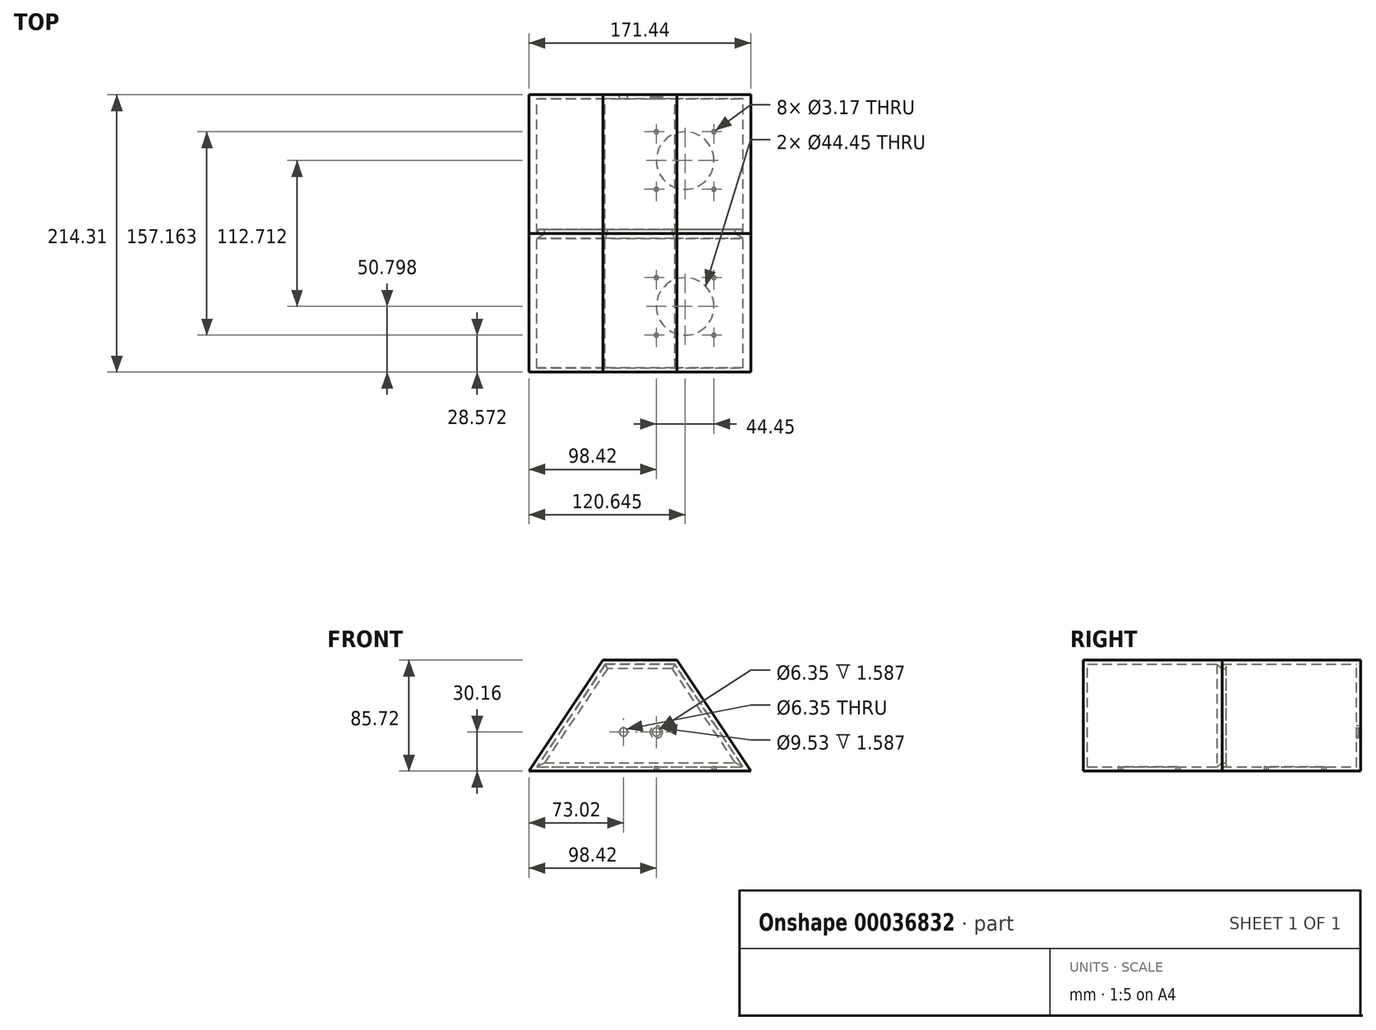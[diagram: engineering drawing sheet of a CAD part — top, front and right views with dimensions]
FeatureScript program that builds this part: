
annotation { "Feature Type Name" : "Feature", "Feature Type Description" : "" }
export const myFeature = defineFeature(function(context is Context, id is Id, definition is map)
    precondition{}
    {
        {
            var Q0;
            Q0=qCreatedBy(makeId("Front.planeOp"),FACE);
            var sketch = newSketch(context, id + "F0", { "sketchPlane" : qUnion([Q0])});
            skLineSegment(sketch, "E0", {"start": v(-85.73, -42.86) * mm, "end": v(85.73, -42.86) * mm});
            skLineSegment(sketch, "E1", {"start": v(85.73, -42.86) * mm, "end": v(28.57, 42.86) * mm});
            skLineSegment(sketch, "E2", {"start": v(28.58, 42.86) * mm, "end": v(-28.58, 42.86) * mm});
            skLineSegment(sketch, "E3", {"start": v(-28.57, 42.86) * mm, "end": v(-85.73, -42.86) * mm});
            skLineSegment(sketch, "E4", {"start": v(0, 42.86) * mm, "end": v(0, -42.86) * mm});
            skPoint(sketch, "E4.endSnap0", {"position": v(0, -42.86) * mm});
            skPoint(sketch, "E5", {"position": v(0, 0) * mm});
            skSolve(sketch);
        }
        {
            var Q0;
            {var subQ2=sQuery(id+"F0.wireOp",EDGE,"E1");Q0=makeQuery(id+"F0.imprint","IMPRINT",FACE,{"disambiguationData":[TD([[makeQuery(id+"F0.imprint","IMPRINT",EDGE,{"derivedFrom":subQ2}),1.0]])]});}
            var Q1;
            {var subQ1=sQuery(id+"F0.wireOp",EDGE,"E3");Q1=makeQuery(id+"F0.imprint","IMPRINT",FACE,{"disambiguationData":[TD([[makeQuery(id+"F0.imprint","IMPRINT",EDGE,{"derivedFrom":subQ1}),1.0]])]});}
            extrude(context, id + "F1", {"entities" : qUnion([Q0, Q1]), "depth" : 214.3 * mm});
        }
        {
            var Q0;
            Q0=makeQuery(id+"F1.opExtrude","CAP_FACE",FACE,{"disambiguationData":[OSD([sQuery(id+"F0.wireOp",EDGE,"E0"),sQuery(id+"F0.wireOp",EDGE,"E1"),sQuery(id+"F0.wireOp",EDGE,"E2"),sQuery(id+"F0.wireOp",EDGE,"E3")])],"isStart":true});
            shell(context, id + "F2", {"entities" : qUnion([Q0]), "thickness" : 3.17 * mm});
        }
        {
            var Q0;
            Q0=qCreatedBy(makeId("Front.planeOp"),FACE);
            var sketch = newSketch(context, id + "F3", { "sketchPlane" : qUnion([Q0])});
            skLineSegment(sketch, "E6.0.0", {"start": v(-28.57, 42.86) * mm, "end": v(28.57, 42.86) * mm});
            skLineSegment(sketch, "E6.0.1", {"start": v(28.57, 42.86) * mm, "end": v(85.72, -42.86) * mm});
            skLineSegment(sketch, "E6.0.2", {"start": v(85.72, -42.86) * mm, "end": v(-85.73, -42.86) * mm});
            skLineSegment(sketch, "E6.0.3", {"start": v(-85.73, -42.86) * mm, "end": v(-28.57, 42.86) * mm});
            skSolve(sketch);
        }
        {
            var Q0;
            Q0 = qSketchRegion(id + "F3", true);
            extrude(context, id + "F4", {"entities" : qUnion([Q0]), "operationType" : NewBodyOperationType.ADD, "depth" : 3.17 * mm});
        }
        {
            var Q0;
            Q0=makeQuery(id+"F1.opExtrude","SWEPT_FACE",FACE,{"disambiguationData":[OSD([sQuery(id+"F0.wireOp",EDGE,"E0")])]});
            var sketch = newSketch(context, id + "F5", { "sketchPlane" : qUnion([Q0])});
            skLineSegment(sketch, "E7", {"start": v(85.72, 214.31) * mm, "end": v(34.92, 214.31) * mm, "construction": true});
            skLineSegment(sketch, "E8", {"start": v(34.92, 214.31) * mm, "end": v(34.92, 163.51) * mm, "construction": true});
            skLineSegment(sketch, "E9", {"start": v(85.72, 0) * mm, "end": v(34.92, 0) * mm, "construction": true});
            skLineSegment(sketch, "E10", {"start": v(34.92, 0) * mm, "end": v(34.92, 50.8) * mm, "construction": true});
            skPoint(sketch, "E11", {"position": v(34.92, 50.8) * mm});
            skPoint(sketch, "E12", {"position": v(34.92, 163.51) * mm});
            skLineSegment(sketch, "E13", {"start": v(34.92, 163.51) * mm, "end": v(57.15, 163.51) * mm, "construction": true});
            skLineSegment(sketch, "E14", {"start": v(57.15, 163.51) * mm, "end": v(57.15, 185.74) * mm, "construction": true});
            skLineSegment(sketch, "E15", {"start": v(57.15, 185.74) * mm, "end": v(12.7, 185.74) * mm, "construction": true});
            skLineSegment(sketch, "E16", {"start": v(12.7, 185.74) * mm, "end": v(12.7, 141.29) * mm, "construction": true});
            skLineSegment(sketch, "E17", {"start": v(12.7, 141.29) * mm, "end": v(57.15, 141.29) * mm, "construction": true});
            skLineSegment(sketch, "E18.rect.bottom", {"start": v(57.15, 28.58) * mm, "end": v(12.7, 28.57) * mm, "construction": true});
            skLineSegment(sketch, "E18.rect.top", {"start": v(57.15, 73.03) * mm, "end": v(12.7, 73.03) * mm, "construction": true});
            skLineSegment(sketch, "E18.rect.left", {"start": v(57.15, 28.58) * mm, "end": v(57.15, 73.03) * mm, "construction": true});
            skLineSegment(sketch, "E18.rect.right", {"start": v(12.7, 28.57) * mm, "end": v(12.7, 73.03) * mm, "construction": true});
            skCircle(sketch, "E19", {"center": v(57.15, 73.03) * mm, "radius": 1.59 * mm});
            skCircle(sketch, "E20", {"center": v(57.15, 28.58) * mm, "radius": 1.59 * mm});
            skCircle(sketch, "E21", {"center": v(12.7, 28.57) * mm, "radius": 1.59 * mm});
            skCircle(sketch, "E22", {"center": v(12.7, 73.03) * mm, "radius": 1.59 * mm});
            skCircle(sketch, "E23", {"center": v(12.7, 185.74) * mm, "radius": 1.59 * mm});
            skCircle(sketch, "E24", {"center": v(57.15, 185.74) * mm, "radius": 1.59 * mm});
            skCircle(sketch, "E25", {"center": v(57.15, 141.29) * mm, "radius": 1.59 * mm});
            skCircle(sketch, "E26", {"center": v(12.7, 141.29) * mm, "radius": 1.59 * mm});
            skSolve(sketch);
        }
        {
            var Q0;
            Q0=sQuery(id+"F5.wireOp",VERTEX,"E11");
            var Q1;
            Q1=sQuery(id+"F5.wireOp",VERTEX,"E12");
            var Q2;
            Q2=makeQuery(id+"F1.opExtrude","SWEPT_BODY",BODY,{"disambiguationData":[OSD([sQuery(id+"F0.wireOp",EDGE,"E0"),sQuery(id+"F0.wireOp",EDGE,"E1"),sQuery(id+"F0.wireOp",EDGE,"E2"),sQuery(id+"F0.wireOp",EDGE,"E3")])]});
            hole(context, id + "F6", {"style" : HoleStyle.SIMPLE, "holeDiameter" : 44.45 * mm, "endStyle" : HoleEndStyle.BLIND, "holeDepth" : 3.17 * mm, "locations" : qUnion([Q0, Q1]), "scope" : qUnion([Q2])});
        }
        {
            var Q0;
            Q0=makeQuery(id+"F4.boolean.opBoolean","MERGE",FACE,{"derivedFrom":[makeQuery(id+"F1.opExtrude","CAP_FACE",FACE,{"disambiguationData":[OSD([sQuery(id+"F0.wireOp",EDGE,"E0"),sQuery(id+"F0.wireOp",EDGE,"E1"),sQuery(id+"F0.wireOp",EDGE,"E2"),sQuery(id+"F0.wireOp",EDGE,"E3")])],"isStart":true}),makeQuery(id+"F4.opExtrude","CAP_FACE",FACE,{"disambiguationData":[OSD([sQuery(id+"F3.wireOp",EDGE,"E6.0.0"),sQuery(id+"F3.wireOp",EDGE,"E6.0.1"),sQuery(id+"F3.wireOp",EDGE,"E6.0.2"),sQuery(id+"F3.wireOp",EDGE,"E6.0.3")])],"isStart":true})]});
            var sketch = newSketch(context, id + "F7", { "sketchPlane" : qUnion([Q0])});
            skCircle(sketch, "E27", {"center": v(12.7, -12.7) * mm, "radius": 3.18 * mm});
            skSolve(sketch);
        }
        {
            var Q0;
            Q0 = qSketchRegion(id + "F7", true);
            extrude(context, id + "F8", {"entities" : qUnion([Q0]), "operationType" : NewBodyOperationType.REMOVE, "oppositeDirection" : true, "depth" : 25.4 * mm});
        }
        {
            var Q0;
            Q0=makeQuery(id+"F4.boolean.opBoolean","MERGE",FACE,{"derivedFrom":[makeQuery(id+"F1.opExtrude","CAP_FACE",FACE,{"disambiguationData":[OSD([sQuery(id+"F0.wireOp",EDGE,"E0"),sQuery(id+"F0.wireOp",EDGE,"E1"),sQuery(id+"F0.wireOp",EDGE,"E2"),sQuery(id+"F0.wireOp",EDGE,"E3")])],"isStart":true}),makeQuery(id+"F4.opExtrude","CAP_FACE",FACE,{"disambiguationData":[OSD([sQuery(id+"F3.wireOp",EDGE,"E6.0.0"),sQuery(id+"F3.wireOp",EDGE,"E6.0.1"),sQuery(id+"F3.wireOp",EDGE,"E6.0.2"),sQuery(id+"F3.wireOp",EDGE,"E6.0.3")])],"isStart":true})]});
            var sketch = newSketch(context, id + "F9", { "sketchPlane" : qUnion([Q0])});
            skCircle(sketch, "E28", {"center": v(-12.7, -12.7) * mm, "radius": 3.18 * mm});
            skSolve(sketch);
        }
        {
            var Q0;
            Q0 = qSketchRegion(id + "F9", true);
            extrude(context, id + "F10", {"entities" : qUnion([Q0]), "operationType" : NewBodyOperationType.REMOVE, "oppositeDirection" : true, "depth" : 25.4 * mm});
        }
        {
            var Q0;
            Q0 = qSketchRegion(id + "F5", true);
            extrude(context, id + "F11", {"entities" : qUnion([Q0]), "operationType" : NewBodyOperationType.REMOVE, "oppositeDirection" : true, "depth" : 12.7 * mm});
        }
        {
            var Q0;
            Q0=makeQuery(id+"F4.opExtrude","CAP_FACE",FACE,{"disambiguationData":[OSD([sQuery(id+"F3.wireOp",EDGE,"E6.0.0"),sQuery(id+"F3.wireOp",EDGE,"E6.0.1"),sQuery(id+"F3.wireOp",EDGE,"E6.0.2"),sQuery(id+"F3.wireOp",EDGE,"E6.0.3")])],"isStart":false});
            var sketch = newSketch(context, id + "F12", { "sketchPlane" : qUnion([Q0])});
            skCircle(sketch, "E29", {"center": v(12.7, -12.7) * mm, "radius": 4.76 * mm});
            skSolve(sketch);
        }
        {
            var Q0;
            Q0=makeQuery(id+"F12.imprint","IMPRINT",FACE,{"disambiguationData":[TD([[makeQuery(id+"F12.imprint","IMPRINT",EDGE,{"derivedFrom":sQuery(id+"F12.wireOp",EDGE,"E29")}),1.0]])]});
            extrude(context, id + "F13", {"entities" : qUnion([Q0]), "operationType" : NewBodyOperationType.REMOVE, "oppositeDirection" : true, "depth" : 1.59 * mm});
        }
        {
            var Q0;
            Q0=makeQuery(id+"F1.opExtrude","SWEPT_FACE",FACE,{"disambiguationData":[OSD([sQuery(id+"F0.wireOp",EDGE,"E0")])]});
            var sketch = newSketch(context, id + "F14", { "sketchPlane" : qUnion([Q0])});
            skLineSegment(sketch, "E30", {"start": v(85.73, 107.17) * mm, "end": v(-85.73, 107.17) * mm});
            skPoint(sketch, "E30.endSnap0", {"position": v(-85.73, 107.16) * mm});
            skLineSegment(sketch, "E31", {"start": v(-85.73, 107.17) * mm, "end": v(-85.73, 107.14) * mm});
            skLineSegment(sketch, "E32", {"start": v(-85.73, 107.14) * mm, "end": v(85.73, 107.14) * mm});
            skLineSegment(sketch, "E33", {"start": v(85.73, 107.14) * mm, "end": v(85.73, 107.17) * mm});
            skPoint(sketch, "E34", {"position": v(85.73, 107.16) * mm});
            skSolve(sketch);
        }
        {
            var Q0;
            Q0 = qSketchRegion(id + "F14", true);
            var Q1;
            Q1=makeQuery(id+"F1.opExtrude","SWEPT_FACE",FACE,{"disambiguationData":[OSD([sQuery(id+"F0.wireOp",EDGE,"E2")])]});
            extrude(context, id + "F15", {"entities" : qUnion([Q0]), "operationType" : NewBodyOperationType.REMOVE, "endBound" : BoundingType.UP_TO_SURFACE, "oppositeDirection" : true, "endBoundEntityFace" : qUnion([Q1]), "depth" : 25.4 * mm});
        }
        {
            var Q0;
            Q0=qCreatedBy(makeId("Right.planeOp"),FACE);
            var sketch = newSketch(context, id + "F16", { "sketchPlane" : qUnion([Q0])});
            skLineSegment(sketch, "E35.0", {"start": v(-211.14, -39.69) * mm, "end": v(-107.17, -39.69) * mm});
            skLineSegment(sketch, "E36", {"start": v(-107.17, -39.69) * mm, "end": v(-107.17, -36.36) * mm});
            skLineSegment(sketch, "E37", {"start": v(-107.17, -36.36) * mm, "end": v(-111.13, -39.69) * mm});
            skLineSegment(sketch, "E38", {"start": v(-107.17, -36.36) * mm, "end": v(-104, -36.36) * mm});
            skLineSegment(sketch, "E39", {"start": v(-104, -36.36) * mm, "end": v(-104, -39.54) * mm});
            skLineSegment(sketch, "E40", {"start": v(-104, -39.54) * mm, "end": v(-107.17, -39.54) * mm});
            skSolve(sketch);
        }
        {
            var Q0;
            {var subQ0=sQuery(id+"F16.wireOp",EDGE,"E37");Q0=makeQuery(id+"F16.imprint","IMPRINT",FACE,{"disambiguationData":[TD([[makeQuery(id+"F16.imprint","IMPRINT",EDGE,{"derivedFrom":subQ0}),1.0]])]});}
            var Q1;
            {var subQ1=sQuery(id+"F16.wireOp",EDGE,"E38");Q1=makeQuery(id+"F16.imprint","IMPRINT",FACE,{"disambiguationData":[TD([[makeQuery(id+"F16.imprint","IMPRINT",EDGE,{"derivedFrom":subQ1}),-1.0]])]});}
            var Q2;
            Q2=makeQuery(id+"F15.boolean.opBoolean","INTERSECT",EDGE,{"derivedFrom":[makeQuery(id+"F2.opShell","OFFSET_FACE",FACE,{"disambiguationData":[OSD([sQuery(id+"F0.wireOp",EDGE,"E0")])]}),makeQuery(id+"F15.opExtrude","SWEPT_FACE",FACE,{"disambiguationData":[OSD([sQuery(id+"F14.wireOp",EDGE,"E30")])]})]});
            var Q3;
            Q3=makeQuery(id+"F15.boolean.opBoolean","INTERSECT",EDGE,{"derivedFrom":[makeQuery(id+"F2.opShell","OFFSET_FACE",FACE,{"disambiguationData":[OSD([sQuery(id+"F0.wireOp",EDGE,"E1")])]}),makeQuery(id+"F15.opExtrude","SWEPT_FACE",FACE,{"disambiguationData":[OSD([sQuery(id+"F14.wireOp",EDGE,"E30")])]})]});
            var Q4;
            Q4=makeQuery(id+"F15.boolean.opBoolean","INTERSECT",EDGE,{"derivedFrom":[makeQuery(id+"F2.opShell","OFFSET_FACE",FACE,{"disambiguationData":[OSD([sQuery(id+"F0.wireOp",EDGE,"E2")])]}),makeQuery(id+"F15.opExtrude","SWEPT_FACE",FACE,{"disambiguationData":[OSD([sQuery(id+"F14.wireOp",EDGE,"E30")])]})]});
            var Q5;
            Q5=makeQuery(id+"F15.boolean.opBoolean","INTERSECT",EDGE,{"derivedFrom":[makeQuery(id+"F2.opShell","OFFSET_FACE",FACE,{"disambiguationData":[OSD([sQuery(id+"F0.wireOp",EDGE,"E3")])]}),makeQuery(id+"F15.opExtrude","SWEPT_FACE",FACE,{"disambiguationData":[OSD([sQuery(id+"F14.wireOp",EDGE,"E30")])]})]});
            sweep(context, id + "F17", {"operationType" : NewBodyOperationType.ADD, "profiles" : qUnion([Q0, Q1]), "path" : qUnion([Q2, Q3, Q4, Q5])});
        }
        {
            var Q0;
            Q0=makeQuery(id+"F17.opSweep","CAP_EDGE",EDGE,{"disambiguationData":[OSD([sQuery(id+"F0.wireOp",EDGE,"E0"),sQuery(id+"F0.wireOp",EDGE,"E1"),sQuery(id+"F14.wireOp",EDGE,"E30"),sQuery(id+"F16.wireOp",EDGE,"E40")])],"isStart":true});
            var Q1;
            Q1=makeQuery(id+"F17.opSweep","MID_CAP_EDGE",EDGE,{"disambiguationData":[OSD([sQuery(id+"F0.wireOp",EDGE,"E1"),sQuery(id+"F0.wireOp",EDGE,"E2"),sQuery(id+"F14.wireOp",EDGE,"E30"),sQuery(id+"F16.wireOp",EDGE,"E40")])],"capPos":3.0});
            var Q2;
            Q2=makeQuery(id+"F17.opSweep","MID_CAP_EDGE",EDGE,{"disambiguationData":[OSD([sQuery(id+"F0.wireOp",EDGE,"E2"),sQuery(id+"F0.wireOp",EDGE,"E3"),sQuery(id+"F14.wireOp",EDGE,"E30"),sQuery(id+"F16.wireOp",EDGE,"E40")])],"capPos":2.0});
            var Q3;
            Q3=makeQuery(id+"F17.opSweep","MID_CAP_EDGE",EDGE,{"disambiguationData":[OSD([sQuery(id+"F0.wireOp",EDGE,"E0"),sQuery(id+"F0.wireOp",EDGE,"E3"),sQuery(id+"F14.wireOp",EDGE,"E30"),sQuery(id+"F16.wireOp",EDGE,"E40")])],"capPos":1.0});
            fillet(context, id + "F18", {"entities" : qUnion([Q0, Q1, Q2, Q3]), "radius" : 0.8 * mm, "tangentPropagation" : true, "allowEdgeOverflow" : false});
        }
    });
